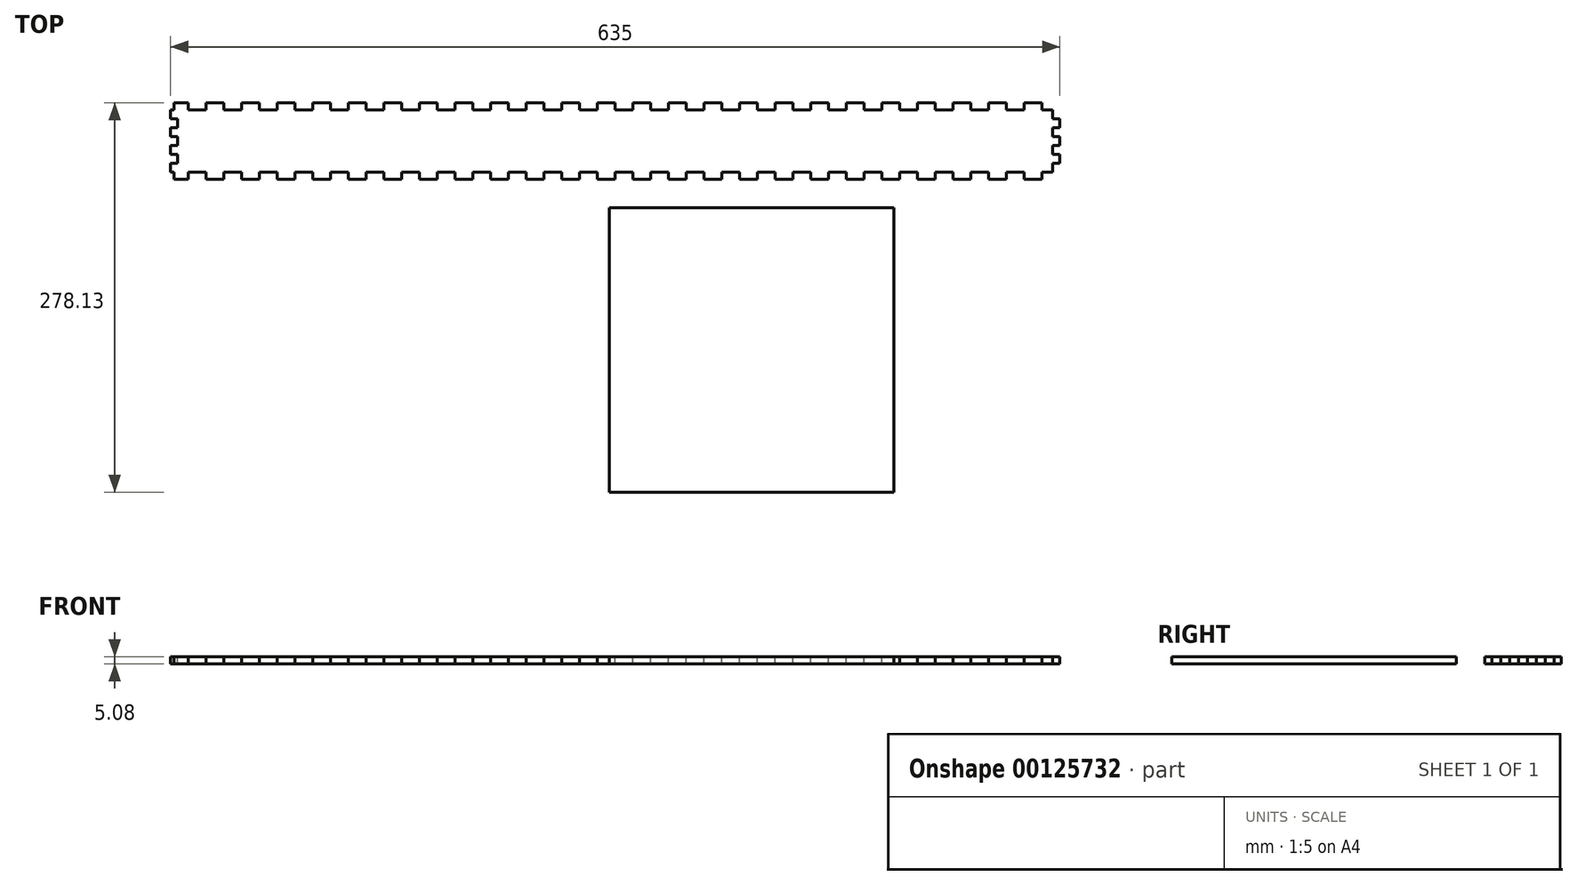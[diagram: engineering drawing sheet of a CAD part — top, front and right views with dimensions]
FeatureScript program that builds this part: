
annotation { "Feature Type Name" : "Feature", "Feature Type Description" : "" }
export const myFeature = defineFeature(function(context is Context, id is Id, definition is map)
    precondition{}
    {
        {
            var Q0;
            Q0=qCreatedBy(makeId("Top.planeOp"),FACE);
            var sketch = newSketch(context, id + "F0", { "sketchPlane" : qUnion([Q0])});
            skLineSegment(sketch, "E0.bottom", {"start": v(-540.54, 29.9) * mm, "end": v(94.46, 29.9) * mm});
            skLineSegment(sketch, "E0.top", {"start": v(-540.54, -24.7) * mm, "end": v(94.46, -24.7) * mm});
            skLineSegment(sketch, "E0.left", {"start": v(-540.54, 29.9) * mm, "end": v(-540.54, -24.7) * mm});
            skLineSegment(sketch, "E0.right", {"start": v(94.46, 29.9) * mm, "end": v(94.46, -24.7) * mm});
            skSolve(sketch);
        }
        {
            var Q0;
            Q0=makeQuery(id+"F0.imprint","IMPRINT",FACE,{"disambiguationData":[TD([[makeQuery(id+"F0.imprint","IMPRINT",EDGE,{"derivedFrom":sQuery(id+"F0.wireOp",EDGE,"E0.bottom")}),-1.0]])]});
            extrude(context, id + "F1", {"entities" : qUnion([Q0]), "depth" : 5.08 * mm});
        }
        {
            var Q0;
            Q0=makeQuery(id+"F1.opExtrude","CAP_FACE",FACE,{"disambiguationData":[OSD([sQuery(id+"F0.wireOp",EDGE,"E0.bottom"),sQuery(id+"F0.wireOp",EDGE,"E0.top"),sQuery(id+"F0.wireOp",EDGE,"E0.left"),sQuery(id+"F0.wireOp",EDGE,"E0.right")])],"isStart":false});
            var sketch = newSketch(context, id + "F2", { "sketchPlane" : qUnion([Q0])});
            skLineSegment(sketch, "E1.0", {"start": v(-540.54, 29.9) * mm, "end": v(94.46, 29.9) * mm});
            skLineSegment(sketch, "E1.1", {"start": v(-540.54, 29.9) * mm, "end": v(-540.54, -24.7) * mm});
            skLineSegment(sketch, "E2", {"start": v(-527.84, 29.9) * mm, "end": v(-527.84, 24.83) * mm});
            skLineSegment(sketch, "E3", {"start": v(-527.84, 24.83) * mm, "end": v(-515.14, 24.83) * mm});
            skLineSegment(sketch, "E4", {"start": v(-515.14, 24.83) * mm, "end": v(-515.14, 29.9) * mm});
            skLineSegment(sketch, "E5.1.0.0", {"start": v(-502.44, 29.9) * mm, "end": v(-502.44, 24.83) * mm});
            skLineSegment(sketch, "E5.1.0.1", {"start": v(-502.44, 24.83) * mm, "end": v(-489.74, 24.83) * mm});
            skLineSegment(sketch, "E5.1.0.2", {"start": v(-489.74, 24.83) * mm, "end": v(-489.74, 29.9) * mm});
            skLineSegment(sketch, "E5.2.0.0", {"start": v(-477.04, 29.9) * mm, "end": v(-477.04, 24.83) * mm});
            skLineSegment(sketch, "E5.2.0.1", {"start": v(-477.04, 24.83) * mm, "end": v(-464.34, 24.83) * mm});
            skLineSegment(sketch, "E5.2.0.2", {"start": v(-464.34, 24.83) * mm, "end": v(-464.34, 29.9) * mm});
            skLineSegment(sketch, "E5.3.0.0", {"start": v(-451.64, 29.9) * mm, "end": v(-451.64, 24.83) * mm});
            skLineSegment(sketch, "E5.3.0.1", {"start": v(-451.64, 24.83) * mm, "end": v(-438.94, 24.83) * mm});
            skLineSegment(sketch, "E5.3.0.2", {"start": v(-438.94, 24.83) * mm, "end": v(-438.94, 29.9) * mm});
            skLineSegment(sketch, "E5.4.0.0", {"start": v(-426.24, 29.9) * mm, "end": v(-426.24, 24.83) * mm});
            skLineSegment(sketch, "E5.4.0.1", {"start": v(-426.24, 24.83) * mm, "end": v(-413.54, 24.83) * mm});
            skLineSegment(sketch, "E5.4.0.2", {"start": v(-413.54, 24.83) * mm, "end": v(-413.54, 29.9) * mm});
            skLineSegment(sketch, "E5.5.0.0", {"start": v(-400.84, 29.9) * mm, "end": v(-400.84, 24.83) * mm});
            skLineSegment(sketch, "E5.5.0.1", {"start": v(-400.84, 24.83) * mm, "end": v(-388.14, 24.83) * mm});
            skLineSegment(sketch, "E5.5.0.2", {"start": v(-388.14, 24.83) * mm, "end": v(-388.14, 29.9) * mm});
            skLineSegment(sketch, "E5.6.0.0", {"start": v(-375.44, 29.9) * mm, "end": v(-375.44, 24.83) * mm});
            skLineSegment(sketch, "E5.6.0.1", {"start": v(-375.44, 24.83) * mm, "end": v(-362.74, 24.83) * mm});
            skLineSegment(sketch, "E5.6.0.2", {"start": v(-362.74, 24.83) * mm, "end": v(-362.74, 29.9) * mm});
            skLineSegment(sketch, "E5.7.0.0", {"start": v(-350.04, 29.9) * mm, "end": v(-350.04, 24.83) * mm});
            skLineSegment(sketch, "E5.7.0.1", {"start": v(-350.04, 24.83) * mm, "end": v(-337.34, 24.83) * mm});
            skLineSegment(sketch, "E5.7.0.2", {"start": v(-337.34, 24.83) * mm, "end": v(-337.34, 29.9) * mm});
            skLineSegment(sketch, "E5.8.0.0", {"start": v(-324.64, 29.9) * mm, "end": v(-324.64, 24.83) * mm});
            skLineSegment(sketch, "E5.8.0.1", {"start": v(-324.64, 24.83) * mm, "end": v(-311.94, 24.83) * mm});
            skLineSegment(sketch, "E5.8.0.2", {"start": v(-311.94, 24.83) * mm, "end": v(-311.94, 29.9) * mm});
            skLineSegment(sketch, "E5.9.0.0", {"start": v(-299.24, 29.9) * mm, "end": v(-299.24, 24.83) * mm});
            skLineSegment(sketch, "E5.9.0.1", {"start": v(-299.24, 24.83) * mm, "end": v(-286.54, 24.83) * mm});
            skLineSegment(sketch, "E5.9.0.2", {"start": v(-286.54, 24.83) * mm, "end": v(-286.54, 29.9) * mm});
            skLineSegment(sketch, "E5.10.0.0", {"start": v(-273.84, 29.9) * mm, "end": v(-273.84, 24.83) * mm});
            skLineSegment(sketch, "E5.10.0.1", {"start": v(-273.84, 24.83) * mm, "end": v(-261.14, 24.83) * mm});
            skLineSegment(sketch, "E5.10.0.2", {"start": v(-261.14, 24.83) * mm, "end": v(-261.14, 29.9) * mm});
            skLineSegment(sketch, "E5.11.0.0", {"start": v(-248.44, 29.9) * mm, "end": v(-248.44, 24.83) * mm});
            skLineSegment(sketch, "E5.11.0.1", {"start": v(-248.44, 24.83) * mm, "end": v(-235.74, 24.83) * mm});
            skLineSegment(sketch, "E5.11.0.2", {"start": v(-235.74, 24.83) * mm, "end": v(-235.74, 29.9) * mm});
            skLineSegment(sketch, "E5.12.0.0", {"start": v(-223.04, 29.9) * mm, "end": v(-223.04, 24.83) * mm});
            skLineSegment(sketch, "E5.12.0.1", {"start": v(-223.04, 24.83) * mm, "end": v(-210.34, 24.83) * mm});
            skLineSegment(sketch, "E5.12.0.2", {"start": v(-210.34, 24.83) * mm, "end": v(-210.34, 29.9) * mm});
            skLineSegment(sketch, "E5.13.0.0", {"start": v(-197.64, 29.9) * mm, "end": v(-197.64, 24.83) * mm});
            skLineSegment(sketch, "E5.13.0.1", {"start": v(-197.64, 24.83) * mm, "end": v(-184.94, 24.83) * mm});
            skLineSegment(sketch, "E5.13.0.2", {"start": v(-184.94, 24.83) * mm, "end": v(-184.94, 29.9) * mm});
            skLineSegment(sketch, "E5.14.0.0", {"start": v(-172.24, 29.9) * mm, "end": v(-172.24, 24.83) * mm});
            skLineSegment(sketch, "E5.14.0.1", {"start": v(-172.24, 24.83) * mm, "end": v(-159.54, 24.83) * mm});
            skLineSegment(sketch, "E5.14.0.2", {"start": v(-159.54, 24.83) * mm, "end": v(-159.54, 29.9) * mm});
            skLineSegment(sketch, "E5.15.0.0", {"start": v(-146.84, 29.9) * mm, "end": v(-146.84, 24.83) * mm});
            skLineSegment(sketch, "E5.15.0.1", {"start": v(-146.84, 24.83) * mm, "end": v(-134.14, 24.83) * mm});
            skLineSegment(sketch, "E5.15.0.2", {"start": v(-134.14, 24.83) * mm, "end": v(-134.14, 29.9) * mm});
            skLineSegment(sketch, "E5.16.0.0", {"start": v(-121.44, 29.9) * mm, "end": v(-121.44, 24.83) * mm});
            skLineSegment(sketch, "E5.16.0.1", {"start": v(-121.44, 24.83) * mm, "end": v(-108.74, 24.83) * mm});
            skLineSegment(sketch, "E5.16.0.2", {"start": v(-108.74, 24.83) * mm, "end": v(-108.74, 29.9) * mm});
            skLineSegment(sketch, "E5.17.0.0", {"start": v(-96.04, 29.9) * mm, "end": v(-96.04, 24.83) * mm});
            skLineSegment(sketch, "E5.17.0.1", {"start": v(-96.04, 24.83) * mm, "end": v(-83.34, 24.83) * mm});
            skLineSegment(sketch, "E5.17.0.2", {"start": v(-83.34, 24.83) * mm, "end": v(-83.34, 29.9) * mm});
            skLineSegment(sketch, "E5.18.0.0", {"start": v(-70.64, 29.9) * mm, "end": v(-70.64, 24.83) * mm});
            skLineSegment(sketch, "E5.18.0.1", {"start": v(-70.64, 24.83) * mm, "end": v(-57.94, 24.83) * mm});
            skLineSegment(sketch, "E5.18.0.2", {"start": v(-57.94, 24.83) * mm, "end": v(-57.94, 29.9) * mm});
            skLineSegment(sketch, "E5.19.0.0", {"start": v(-45.24, 29.9) * mm, "end": v(-45.24, 24.83) * mm});
            skLineSegment(sketch, "E5.19.0.1", {"start": v(-45.24, 24.83) * mm, "end": v(-32.54, 24.83) * mm});
            skLineSegment(sketch, "E5.19.0.2", {"start": v(-32.54, 24.83) * mm, "end": v(-32.54, 29.9) * mm});
            skLineSegment(sketch, "E5.20.0.0", {"start": v(-19.84, 29.9) * mm, "end": v(-19.84, 24.83) * mm});
            skLineSegment(sketch, "E5.20.0.1", {"start": v(-19.84, 24.83) * mm, "end": v(-7.14, 24.83) * mm});
            skLineSegment(sketch, "E5.20.0.2", {"start": v(-7.14, 24.83) * mm, "end": v(-7.14, 29.9) * mm});
            skLineSegment(sketch, "E5.21.0.0", {"start": v(5.56, 29.9) * mm, "end": v(5.56, 24.83) * mm});
            skLineSegment(sketch, "E5.21.0.1", {"start": v(5.56, 24.83) * mm, "end": v(18.26, 24.83) * mm});
            skLineSegment(sketch, "E5.21.0.2", {"start": v(18.26, 24.83) * mm, "end": v(18.26, 29.9) * mm});
            skLineSegment(sketch, "E5.22.0.0", {"start": v(30.96, 29.9) * mm, "end": v(30.96, 24.83) * mm});
            skLineSegment(sketch, "E5.22.0.1", {"start": v(30.96, 24.83) * mm, "end": v(43.66, 24.83) * mm});
            skLineSegment(sketch, "E5.22.0.2", {"start": v(43.66, 24.83) * mm, "end": v(43.66, 29.9) * mm});
            skLineSegment(sketch, "E5.23.0.0", {"start": v(56.36, 29.9) * mm, "end": v(56.36, 24.83) * mm});
            skLineSegment(sketch, "E5.23.0.1", {"start": v(56.36, 24.83) * mm, "end": v(69.06, 24.83) * mm});
            skLineSegment(sketch, "E5.23.0.2", {"start": v(69.06, 24.83) * mm, "end": v(69.06, 29.9) * mm});
            skLineSegment(sketch, "E5.24.0.0", {"start": v(81.76, 29.9) * mm, "end": v(81.76, 24.83) * mm});
            skLineSegment(sketch, "E5.24.0.1", {"start": v(81.76, 24.83) * mm, "end": v(94.46, 24.83) * mm});
            skLineSegment(sketch, "E5.24.0.2", {"start": v(94.46, 24.83) * mm, "end": v(94.46, 29.9) * mm});
            skLineSegment(sketch, "E5.direction1", {"start": v(-527.84, 24.83) * mm, "end": v(-502.44, 24.83) * mm, "construction": true});
            skLineSegment(sketch, "E6", {"start": v(-540.54, 18.48) * mm, "end": v(-535.46, 18.48) * mm});
            skLineSegment(sketch, "E7", {"start": v(-535.46, 18.48) * mm, "end": v(-535.46, 12.13) * mm});
            skLineSegment(sketch, "E8", {"start": v(-535.46, 12.13) * mm, "end": v(-540.54, 12.13) * mm});
            skLineSegment(sketch, "E9.0.1.0", {"start": v(-540.54, 5.78) * mm, "end": v(-535.46, 5.78) * mm});
            skLineSegment(sketch, "E9.0.1.1", {"start": v(-535.46, 5.78) * mm, "end": v(-535.46, -0.57) * mm});
            skLineSegment(sketch, "E9.0.1.2", {"start": v(-535.46, -0.57) * mm, "end": v(-540.54, -0.57) * mm});
            skLineSegment(sketch, "E9.0.2.0", {"start": v(-540.54, -6.92) * mm, "end": v(-535.46, -6.92) * mm});
            skLineSegment(sketch, "E9.0.2.1", {"start": v(-535.46, -6.92) * mm, "end": v(-535.46, -13.27) * mm});
            skLineSegment(sketch, "E9.0.2.2", {"start": v(-535.46, -13.27) * mm, "end": v(-540.54, -13.27) * mm});
            skLineSegment(sketch, "E9.direction1", {"start": v(-540.54, 12.13) * mm, "end": v(-515.14, 12.13) * mm, "construction": true});
            skLineSegment(sketch, "E9.direction2", {"start": v(-540.54, 12.13) * mm, "end": v(-540.54, -0.57) * mm, "construction": true});
            skLineSegment(sketch, "E10", {"start": v(-540.54, 2.6) * mm, "end": v(-455.77, 2.6) * mm, "construction": true});
            skPoint(sketch, "E10.endSnap0", {"position": v(-535.46, 2.6) * mm});
            skLineSegment(sketch, "E11.MirrorCS", {"start": v(-502.44, -24.7) * mm, "end": v(-502.44, -19.62) * mm});
            skLineSegment(sketch, "E12.MirrorCS", {"start": v(-502.44, -19.62) * mm, "end": v(-489.74, -19.62) * mm});
            skLineSegment(sketch, "E13.MirrorCS", {"start": v(-489.74, -19.62) * mm, "end": v(-489.74, -24.7) * mm});
            skLineSegment(sketch, "E14.MirrorCS", {"start": v(-515.14, -19.62) * mm, "end": v(-515.14, -24.7) * mm});
            skLineSegment(sketch, "E15.MirrorCS", {"start": v(-527.84, -24.7) * mm, "end": v(-527.84, -19.62) * mm});
            skLineSegment(sketch, "E16.MirrorCS", {"start": v(-477.04, -24.7) * mm, "end": v(-477.04, -19.62) * mm});
            skLineSegment(sketch, "E17.MirrorCS", {"start": v(-477.04, -19.62) * mm, "end": v(-464.34, -19.62) * mm});
            skLineSegment(sketch, "E18.MirrorCS", {"start": v(-464.34, -19.62) * mm, "end": v(-464.34, -24.7) * mm});
            skLineSegment(sketch, "E19", {"start": v(-527.84, -19.62) * mm, "end": v(-515.14, -19.62) * mm});
            skLineSegment(sketch, "E20.MirrorCS", {"start": v(18.26, -19.62) * mm, "end": v(18.26, -24.7) * mm});
            skLineSegment(sketch, "E21.MirrorCS", {"start": v(-184.94, -19.62) * mm, "end": v(-184.94, -24.7) * mm});
            skLineSegment(sketch, "E22.MirrorCS", {"start": v(-45.24, -24.7) * mm, "end": v(-45.24, -19.62) * mm});
            skLineSegment(sketch, "E23.MirrorCS", {"start": v(-299.24, -24.7) * mm, "end": v(-299.24, -19.62) * mm});
            skLineSegment(sketch, "E24.MirrorCS", {"start": v(-375.44, -24.7) * mm, "end": v(-375.44, -19.62) * mm});
            skLineSegment(sketch, "E25.MirrorCS", {"start": v(-121.44, -24.7) * mm, "end": v(-121.44, -19.62) * mm});
            skLineSegment(sketch, "E26.MirrorCS", {"start": v(-388.14, -19.62) * mm, "end": v(-388.14, -24.7) * mm});
            skLineSegment(sketch, "E27.MirrorCS", {"start": v(-261.14, -19.62) * mm, "end": v(-261.14, -24.7) * mm});
            skLineSegment(sketch, "E28.MirrorCS", {"start": v(-197.64, -24.7) * mm, "end": v(-197.64, -19.62) * mm});
            skLineSegment(sketch, "E29.MirrorCS", {"start": v(-337.34, -19.62) * mm, "end": v(-337.34, -24.7) * mm});
            skLineSegment(sketch, "E30.MirrorCS", {"start": v(69.06, -19.62) * mm, "end": v(69.06, -24.7) * mm});
            skLineSegment(sketch, "E31.MirrorCS", {"start": v(-451.64, -24.7) * mm, "end": v(-451.64, -19.62) * mm});
            skLineSegment(sketch, "E32.MirrorCS", {"start": v(-426.24, -24.7) * mm, "end": v(-426.24, -19.62) * mm});
            skLineSegment(sketch, "E33.MirrorCS", {"start": v(-438.94, -19.62) * mm, "end": v(-438.94, -24.7) * mm});
            skLineSegment(sketch, "E34.MirrorCS", {"start": v(5.56, -24.7) * mm, "end": v(5.56, -19.62) * mm});
            skLineSegment(sketch, "E35.MirrorCS", {"start": v(-134.14, -19.62) * mm, "end": v(-134.14, -24.7) * mm});
            skLineSegment(sketch, "E36.MirrorCS", {"start": v(-400.84, -24.7) * mm, "end": v(-400.84, -19.62) * mm});
            skLineSegment(sketch, "E37.MirrorCS", {"start": v(-210.34, -19.62) * mm, "end": v(-210.34, -24.7) * mm});
            skLineSegment(sketch, "E38.MirrorCS", {"start": v(-70.64, -24.7) * mm, "end": v(-70.64, -19.62) * mm});
            skLineSegment(sketch, "E39.MirrorCS", {"start": v(-413.54, -19.62) * mm, "end": v(-413.54, -24.7) * mm});
            skLineSegment(sketch, "E40.MirrorCS", {"start": v(-273.84, -24.7) * mm, "end": v(-273.84, -19.62) * mm});
            skLineSegment(sketch, "E41.MirrorCS", {"start": v(-350.04, -24.7) * mm, "end": v(-350.04, -19.62) * mm});
            skLineSegment(sketch, "E42.MirrorCS", {"start": v(-83.34, -19.62) * mm, "end": v(-83.34, -24.7) * mm});
            skLineSegment(sketch, "E43.MirrorCS", {"start": v(56.36, -24.7) * mm, "end": v(56.36, -19.62) * mm});
            skLineSegment(sketch, "E44.MirrorCS", {"start": v(-7.14, -19.62) * mm, "end": v(-7.14, -24.7) * mm});
            skLineSegment(sketch, "E45.MirrorCS", {"start": v(43.66, -19.62) * mm, "end": v(43.66, -24.7) * mm});
            skLineSegment(sketch, "E46.MirrorCS", {"start": v(-146.84, -24.7) * mm, "end": v(-146.84, -19.62) * mm});
            skLineSegment(sketch, "E47.MirrorCS", {"start": v(-286.54, -19.62) * mm, "end": v(-286.54, -24.7) * mm});
            skLineSegment(sketch, "E48.MirrorCS", {"start": v(-223.04, -24.7) * mm, "end": v(-223.04, -19.62) * mm});
            skLineSegment(sketch, "E49.MirrorCS", {"start": v(-362.74, -19.62) * mm, "end": v(-362.74, -24.7) * mm});
            skLineSegment(sketch, "E50.MirrorCS", {"start": v(-159.54, -19.62) * mm, "end": v(-159.54, -24.7) * mm});
            skLineSegment(sketch, "E51.MirrorCS", {"start": v(-19.84, -24.7) * mm, "end": v(-19.84, -19.62) * mm});
            skLineSegment(sketch, "E52.MirrorCS", {"start": v(-96.04, -24.7) * mm, "end": v(-96.04, -19.62) * mm});
            skLineSegment(sketch, "E53.MirrorCS", {"start": v(-248.44, -24.7) * mm, "end": v(-248.44, -19.62) * mm});
            skLineSegment(sketch, "E54.MirrorCS", {"start": v(81.76, -24.7) * mm, "end": v(81.76, -19.62) * mm});
            skLineSegment(sketch, "E55.MirrorCS", {"start": v(-311.94, -19.62) * mm, "end": v(-311.94, -24.7) * mm});
            skLineSegment(sketch, "E56.MirrorCS", {"start": v(-235.74, -19.62) * mm, "end": v(-235.74, -24.7) * mm});
            skLineSegment(sketch, "E57.MirrorCS", {"start": v(-172.24, -24.7) * mm, "end": v(-172.24, -19.62) * mm});
            skLineSegment(sketch, "E58.MirrorCS", {"start": v(-57.94, -19.62) * mm, "end": v(-57.94, -24.7) * mm});
            skLineSegment(sketch, "E59.MirrorCS", {"start": v(94.46, -19.62) * mm, "end": v(94.46, -24.7) * mm});
            skLineSegment(sketch, "E60.MirrorCS", {"start": v(-324.64, -24.7) * mm, "end": v(-324.64, -19.62) * mm});
            skLineSegment(sketch, "E61.MirrorCS", {"start": v(-108.74, -19.62) * mm, "end": v(-108.74, -24.7) * mm});
            skLineSegment(sketch, "E62.MirrorCS", {"start": v(30.96, -24.7) * mm, "end": v(30.96, -19.62) * mm});
            skLineSegment(sketch, "E63.MirrorCS", {"start": v(-32.54, -19.62) * mm, "end": v(-32.54, -24.7) * mm});
            skLineSegment(sketch, "E64.MirrorCS", {"start": v(-121.44, -19.62) * mm, "end": v(-108.74, -19.62) * mm});
            skLineSegment(sketch, "E65.MirrorCS", {"start": v(-324.64, -19.62) * mm, "end": v(-311.94, -19.62) * mm});
            skLineSegment(sketch, "E66.MirrorCS", {"start": v(-248.44, -19.62) * mm, "end": v(-235.74, -19.62) * mm});
            skLineSegment(sketch, "E67.MirrorCS", {"start": v(5.56, -19.62) * mm, "end": v(18.26, -19.62) * mm});
            skLineSegment(sketch, "E68.MirrorCS", {"start": v(-400.84, -19.62) * mm, "end": v(-388.14, -19.62) * mm});
            skLineSegment(sketch, "E69.MirrorCS", {"start": v(-451.64, -19.62) * mm, "end": v(-438.94, -19.62) * mm});
            skLineSegment(sketch, "E70.MirrorCS", {"start": v(-70.64, -19.62) * mm, "end": v(-57.94, -19.62) * mm});
            skLineSegment(sketch, "E71.MirrorCS", {"start": v(-426.24, -19.62) * mm, "end": v(-413.54, -19.62) * mm});
            skLineSegment(sketch, "E72.MirrorCS", {"start": v(-273.84, -19.62) * mm, "end": v(-261.14, -19.62) * mm});
            skLineSegment(sketch, "E73.MirrorCS", {"start": v(-350.04, -19.62) * mm, "end": v(-337.34, -19.62) * mm});
            skLineSegment(sketch, "E74.MirrorCS", {"start": v(56.36, -19.62) * mm, "end": v(69.06, -19.62) * mm});
            skLineSegment(sketch, "E75.MirrorCS", {"start": v(-223.04, -19.62) * mm, "end": v(-210.34, -19.62) * mm});
            skLineSegment(sketch, "E76.MirrorCS", {"start": v(-146.84, -19.62) * mm, "end": v(-134.14, -19.62) * mm});
            skLineSegment(sketch, "E77.MirrorCS", {"start": v(-96.04, -19.62) * mm, "end": v(-83.34, -19.62) * mm});
            skLineSegment(sketch, "E78.MirrorCS", {"start": v(-19.84, -19.62) * mm, "end": v(-7.14, -19.62) * mm});
            skLineSegment(sketch, "E79.MirrorCS", {"start": v(81.76, -19.62) * mm, "end": v(94.46, -19.62) * mm});
            skLineSegment(sketch, "E80.MirrorCS", {"start": v(30.96, -19.62) * mm, "end": v(43.66, -19.62) * mm});
            skLineSegment(sketch, "E81.MirrorCS", {"start": v(-375.44, -19.62) * mm, "end": v(-362.74, -19.62) * mm});
            skLineSegment(sketch, "E82.MirrorCS", {"start": v(-299.24, -19.62) * mm, "end": v(-286.54, -19.62) * mm});
            skLineSegment(sketch, "E83.MirrorCS", {"start": v(-45.24, -19.62) * mm, "end": v(-32.54, -19.62) * mm});
            skLineSegment(sketch, "E84.MirrorCS", {"start": v(-172.24, -19.62) * mm, "end": v(-159.54, -19.62) * mm});
            skLineSegment(sketch, "E85.MirrorCS", {"start": v(-197.64, -19.62) * mm, "end": v(-184.94, -19.62) * mm});
            skLineSegment(sketch, "E86", {"start": v(-223.04, 29.9) * mm, "end": v(-223.04, -38.72) * mm, "construction": true});
            skLineSegment(sketch, "E87.MirrorCS", {"start": v(89.38, -13.27) * mm, "end": v(94.46, -13.27) * mm});
            skLineSegment(sketch, "E88.MirrorCS", {"start": v(94.46, -6.92) * mm, "end": v(89.38, -6.92) * mm});
            skLineSegment(sketch, "E89.MirrorCS", {"start": v(89.38, -0.57) * mm, "end": v(94.46, -0.57) * mm});
            skLineSegment(sketch, "E90.MirrorCS", {"start": v(94.46, 5.78) * mm, "end": v(89.38, 5.78) * mm});
            skLineSegment(sketch, "E91.MirrorCS", {"start": v(94.46, 18.48) * mm, "end": v(89.38, 18.48) * mm});
            skLineSegment(sketch, "E92", {"start": v(89.38, 12.13) * mm, "end": v(94.46, 12.13) * mm});
            skLineSegment(sketch, "E93", {"start": v(89.38, 12.13) * mm, "end": v(89.38, 5.78) * mm});
            skLineSegment(sketch, "E94", {"start": v(89.38, -0.57) * mm, "end": v(89.38, -6.92) * mm});
            skLineSegment(sketch, "E95", {"start": v(89.38, -13.27) * mm, "end": v(89.38, -19.62) * mm});
            skLineSegment(sketch, "E96", {"start": v(89.38, 18.48) * mm, "end": v(89.38, 24.83) * mm});
            skLineSegment(sketch, "E97", {"start": v(-464.34, -24.7) * mm, "end": v(-451.64, -24.7) * mm});
            skLineSegment(sketch, "E98", {"start": v(-538, 29.9) * mm, "end": v(-538, 24.83) * mm});
            skLineSegment(sketch, "E99", {"start": v(-538, 24.83) * mm, "end": v(-540.54, 24.83) * mm});
            skLineSegment(sketch, "E100.MirrorCS", {"start": v(-538, -24.7) * mm, "end": v(-538, -19.62) * mm});
            skLineSegment(sketch, "E101.MirrorCS", {"start": v(-538, -19.62) * mm, "end": v(-540.54, -19.62) * mm});
            skSolve(sketch);
        }
        {
            var Q0;
            {var subQ0=sQuery(id+"F2.wireOp",EDGE,"E6");Q0=makeQuery(id+"F2.imprint","IMPRINT",FACE,{"disambiguationData":[TD([[makeQuery(id+"F2.imprint","IMPRINT",EDGE,{"derivedFrom":subQ0}),-1.0]])]});}
            var Q1;
            {var subQ0=sQuery(id+"F2.wireOp",EDGE,"E9.0.1.0");Q1=makeQuery(id+"F2.imprint","IMPRINT",FACE,{"disambiguationData":[TD([[makeQuery(id+"F2.imprint","IMPRINT",EDGE,{"derivedFrom":subQ0}),-1.0]])]});}
            var Q2;
            {var subQ0=sQuery(id+"F2.wireOp",EDGE,"E9.0.2.0");Q2=makeQuery(id+"F2.imprint","IMPRINT",FACE,{"disambiguationData":[TD([[makeQuery(id+"F2.imprint","IMPRINT",EDGE,{"derivedFrom":subQ0}),-1.0]])]});}
            var Q3;
            {var subQ0=sQuery(id+"F2.wireOp",EDGE,"E2");Q3=makeQuery(id+"F2.imprint","IMPRINT",FACE,{"disambiguationData":[TD([[makeQuery(id+"F2.imprint","IMPRINT",EDGE,{"derivedFrom":subQ0}),1.0]])]});}
            var Q4;
            {var subQ0=sQuery(id+"F2.wireOp",EDGE,"E5.1.0.0");Q4=makeQuery(id+"F2.imprint","IMPRINT",FACE,{"disambiguationData":[TD([[makeQuery(id+"F2.imprint","IMPRINT",EDGE,{"derivedFrom":subQ0}),1.0]])]});}
            var Q5;
            {var subQ0=sQuery(id+"F2.wireOp",EDGE,"E14.MirrorCS");Q5=makeQuery(id+"F2.imprint","IMPRINT",FACE,{"disambiguationData":[TD([[makeQuery(id+"F2.imprint","IMPRINT",EDGE,{"derivedFrom":subQ0}),-1.0]])]});}
            var Q6;
            {var subQ0=sQuery(id+"F2.wireOp",EDGE,"E11.MirrorCS");Q6=makeQuery(id+"F2.imprint","IMPRINT",FACE,{"disambiguationData":[TD([[makeQuery(id+"F2.imprint","IMPRINT",EDGE,{"derivedFrom":subQ0}),-1.0]])]});}
            var Q7;
            {var subQ0=sQuery(id+"F2.wireOp",EDGE,"E5.2.0.0");Q7=makeQuery(id+"F2.imprint","IMPRINT",FACE,{"disambiguationData":[TD([[makeQuery(id+"F2.imprint","IMPRINT",EDGE,{"derivedFrom":subQ0}),1.0]])]});}
            var Q8;
            {var subQ0=sQuery(id+"F2.wireOp",EDGE,"E16.MirrorCS");Q8=makeQuery(id+"F2.imprint","IMPRINT",FACE,{"disambiguationData":[TD([[makeQuery(id+"F2.imprint","IMPRINT",EDGE,{"derivedFrom":subQ0}),-1.0]])]});}
            var Q9;
            {var subQ0=sQuery(id+"F2.wireOp",EDGE,"E31.MirrorCS");Q9=makeQuery(id+"F2.imprint","IMPRINT",FACE,{"disambiguationData":[TD([[makeQuery(id+"F2.imprint","IMPRINT",EDGE,{"derivedFrom":subQ0}),-1.0]])]});}
            var Q10;
            {var subQ0=sQuery(id+"F2.wireOp",EDGE,"E5.3.0.0");Q10=makeQuery(id+"F2.imprint","IMPRINT",FACE,{"disambiguationData":[TD([[makeQuery(id+"F2.imprint","IMPRINT",EDGE,{"derivedFrom":subQ0}),1.0]])]});}
            var Q11;
            {var subQ0=sQuery(id+"F2.wireOp",EDGE,"E5.4.0.0");Q11=makeQuery(id+"F2.imprint","IMPRINT",FACE,{"disambiguationData":[TD([[makeQuery(id+"F2.imprint","IMPRINT",EDGE,{"derivedFrom":subQ0}),1.0]])]});}
            var Q12;
            {var subQ0=sQuery(id+"F2.wireOp",EDGE,"E32.MirrorCS");Q12=makeQuery(id+"F2.imprint","IMPRINT",FACE,{"disambiguationData":[TD([[makeQuery(id+"F2.imprint","IMPRINT",EDGE,{"derivedFrom":subQ0}),-1.0]])]});}
            var Q13;
            {var subQ0=sQuery(id+"F2.wireOp",EDGE,"E26.MirrorCS");Q13=makeQuery(id+"F2.imprint","IMPRINT",FACE,{"disambiguationData":[TD([[makeQuery(id+"F2.imprint","IMPRINT",EDGE,{"derivedFrom":subQ0}),-1.0]])]});}
            var Q14;
            {var subQ0=sQuery(id+"F2.wireOp",EDGE,"E5.5.0.0");Q14=makeQuery(id+"F2.imprint","IMPRINT",FACE,{"disambiguationData":[TD([[makeQuery(id+"F2.imprint","IMPRINT",EDGE,{"derivedFrom":subQ0}),1.0]])]});}
            var Q15;
            {var subQ0=sQuery(id+"F2.wireOp",EDGE,"E5.6.0.0");Q15=makeQuery(id+"F2.imprint","IMPRINT",FACE,{"disambiguationData":[TD([[makeQuery(id+"F2.imprint","IMPRINT",EDGE,{"derivedFrom":subQ0}),1.0]])]});}
            var Q16;
            {var subQ0=sQuery(id+"F2.wireOp",EDGE,"E24.MirrorCS");Q16=makeQuery(id+"F2.imprint","IMPRINT",FACE,{"disambiguationData":[TD([[makeQuery(id+"F2.imprint","IMPRINT",EDGE,{"derivedFrom":subQ0}),-1.0]])]});}
            var Q17;
            {var subQ0=sQuery(id+"F2.wireOp",EDGE,"E29.MirrorCS");Q17=makeQuery(id+"F2.imprint","IMPRINT",FACE,{"disambiguationData":[TD([[makeQuery(id+"F2.imprint","IMPRINT",EDGE,{"derivedFrom":subQ0}),-1.0]])]});}
            var Q18;
            {var subQ0=sQuery(id+"F2.wireOp",EDGE,"E5.7.0.0");Q18=makeQuery(id+"F2.imprint","IMPRINT",FACE,{"disambiguationData":[TD([[makeQuery(id+"F2.imprint","IMPRINT",EDGE,{"derivedFrom":subQ0}),1.0]])]});}
            var Q19;
            {var subQ0=sQuery(id+"F2.wireOp",EDGE,"E5.8.0.0");Q19=makeQuery(id+"F2.imprint","IMPRINT",FACE,{"disambiguationData":[TD([[makeQuery(id+"F2.imprint","IMPRINT",EDGE,{"derivedFrom":subQ0}),1.0]])]});}
            var Q20;
            {var subQ0=sQuery(id+"F2.wireOp",EDGE,"E55.MirrorCS");Q20=makeQuery(id+"F2.imprint","IMPRINT",FACE,{"disambiguationData":[TD([[makeQuery(id+"F2.imprint","IMPRINT",EDGE,{"derivedFrom":subQ0}),-1.0]])]});}
            var Q21;
            {var subQ0=sQuery(id+"F2.wireOp",EDGE,"E23.MirrorCS");Q21=makeQuery(id+"F2.imprint","IMPRINT",FACE,{"disambiguationData":[TD([[makeQuery(id+"F2.imprint","IMPRINT",EDGE,{"derivedFrom":subQ0}),-1.0]])]});}
            var Q22;
            {var subQ0=sQuery(id+"F2.wireOp",EDGE,"E5.9.0.0");Q22=makeQuery(id+"F2.imprint","IMPRINT",FACE,{"disambiguationData":[TD([[makeQuery(id+"F2.imprint","IMPRINT",EDGE,{"derivedFrom":subQ0}),1.0]])]});}
            var Q23;
            {var subQ0=sQuery(id+"F2.wireOp",EDGE,"E5.10.0.0");Q23=makeQuery(id+"F2.imprint","IMPRINT",FACE,{"disambiguationData":[TD([[makeQuery(id+"F2.imprint","IMPRINT",EDGE,{"derivedFrom":subQ0}),1.0]])]});}
            var Q24;
            {var subQ0=sQuery(id+"F2.wireOp",EDGE,"E27.MirrorCS");Q24=makeQuery(id+"F2.imprint","IMPRINT",FACE,{"disambiguationData":[TD([[makeQuery(id+"F2.imprint","IMPRINT",EDGE,{"derivedFrom":subQ0}),-1.0]])]});}
            var Q25;
            {var subQ0=sQuery(id+"F2.wireOp",EDGE,"E53.MirrorCS");Q25=makeQuery(id+"F2.imprint","IMPRINT",FACE,{"disambiguationData":[TD([[makeQuery(id+"F2.imprint","IMPRINT",EDGE,{"derivedFrom":subQ0}),-1.0]])]});}
            var Q26;
            {var subQ0=sQuery(id+"F2.wireOp",EDGE,"E5.11.0.0");Q26=makeQuery(id+"F2.imprint","IMPRINT",FACE,{"disambiguationData":[TD([[makeQuery(id+"F2.imprint","IMPRINT",EDGE,{"derivedFrom":subQ0}),1.0]])]});}
            var Q27;
            {var subQ0=sQuery(id+"F2.wireOp",EDGE,"E5.12.0.0");Q27=makeQuery(id+"F2.imprint","IMPRINT",FACE,{"disambiguationData":[TD([[makeQuery(id+"F2.imprint","IMPRINT",EDGE,{"derivedFrom":subQ0}),1.0]])]});}
            var Q28;
            {var subQ0=sQuery(id+"F2.wireOp",EDGE,"E37.MirrorCS");Q28=makeQuery(id+"F2.imprint","IMPRINT",FACE,{"disambiguationData":[TD([[makeQuery(id+"F2.imprint","IMPRINT",EDGE,{"derivedFrom":subQ0}),-1.0]])]});}
            var Q29;
            {var subQ0=sQuery(id+"F2.wireOp",EDGE,"E5.13.0.0");Q29=makeQuery(id+"F2.imprint","IMPRINT",FACE,{"disambiguationData":[TD([[makeQuery(id+"F2.imprint","IMPRINT",EDGE,{"derivedFrom":subQ0}),1.0]])]});}
            var Q30;
            {var subQ0=sQuery(id+"F2.wireOp",EDGE,"E21.MirrorCS");Q30=makeQuery(id+"F2.imprint","IMPRINT",FACE,{"disambiguationData":[TD([[makeQuery(id+"F2.imprint","IMPRINT",EDGE,{"derivedFrom":subQ0}),-1.0]])]});}
            var Q31;
            {var subQ0=sQuery(id+"F2.wireOp",EDGE,"E50.MirrorCS");Q31=makeQuery(id+"F2.imprint","IMPRINT",FACE,{"disambiguationData":[TD([[makeQuery(id+"F2.imprint","IMPRINT",EDGE,{"derivedFrom":subQ0}),-1.0]])]});}
            var Q32;
            {var subQ0=sQuery(id+"F2.wireOp",EDGE,"E5.14.0.0");Q32=makeQuery(id+"F2.imprint","IMPRINT",FACE,{"disambiguationData":[TD([[makeQuery(id+"F2.imprint","IMPRINT",EDGE,{"derivedFrom":subQ0}),1.0]])]});}
            var Q33;
            {var subQ0=sQuery(id+"F2.wireOp",EDGE,"E5.15.0.0");Q33=makeQuery(id+"F2.imprint","IMPRINT",FACE,{"disambiguationData":[TD([[makeQuery(id+"F2.imprint","IMPRINT",EDGE,{"derivedFrom":subQ0}),1.0]])]});}
            var Q34;
            {var subQ0=sQuery(id+"F2.wireOp",EDGE,"E35.MirrorCS");Q34=makeQuery(id+"F2.imprint","IMPRINT",FACE,{"disambiguationData":[TD([[makeQuery(id+"F2.imprint","IMPRINT",EDGE,{"derivedFrom":subQ0}),-1.0]])]});}
            var Q35;
            {var subQ0=sQuery(id+"F2.wireOp",EDGE,"E25.MirrorCS");Q35=makeQuery(id+"F2.imprint","IMPRINT",FACE,{"disambiguationData":[TD([[makeQuery(id+"F2.imprint","IMPRINT",EDGE,{"derivedFrom":subQ0}),-1.0]])]});}
            var Q36;
            {var subQ0=sQuery(id+"F2.wireOp",EDGE,"E5.16.0.0");Q36=makeQuery(id+"F2.imprint","IMPRINT",FACE,{"disambiguationData":[TD([[makeQuery(id+"F2.imprint","IMPRINT",EDGE,{"derivedFrom":subQ0}),1.0]])]});}
            var Q37;
            {var subQ0=sQuery(id+"F2.wireOp",EDGE,"E42.MirrorCS");Q37=makeQuery(id+"F2.imprint","IMPRINT",FACE,{"disambiguationData":[TD([[makeQuery(id+"F2.imprint","IMPRINT",EDGE,{"derivedFrom":subQ0}),-1.0]])]});}
            var Q38;
            {var subQ0=sQuery(id+"F2.wireOp",EDGE,"E5.17.0.0");Q38=makeQuery(id+"F2.imprint","IMPRINT",FACE,{"disambiguationData":[TD([[makeQuery(id+"F2.imprint","IMPRINT",EDGE,{"derivedFrom":subQ0}),1.0]])]});}
            var Q39;
            {var subQ0=sQuery(id+"F2.wireOp",EDGE,"E38.MirrorCS");Q39=makeQuery(id+"F2.imprint","IMPRINT",FACE,{"disambiguationData":[TD([[makeQuery(id+"F2.imprint","IMPRINT",EDGE,{"derivedFrom":subQ0}),-1.0]])]});}
            var Q40;
            {var subQ0=sQuery(id+"F2.wireOp",EDGE,"E5.18.0.0");Q40=makeQuery(id+"F2.imprint","IMPRINT",FACE,{"disambiguationData":[TD([[makeQuery(id+"F2.imprint","IMPRINT",EDGE,{"derivedFrom":subQ0}),1.0]])]});}
            var Q41;
            {var subQ0=sQuery(id+"F2.wireOp",EDGE,"E5.19.0.0");Q41=makeQuery(id+"F2.imprint","IMPRINT",FACE,{"disambiguationData":[TD([[makeQuery(id+"F2.imprint","IMPRINT",EDGE,{"derivedFrom":subQ0}),1.0]])]});}
            var Q42;
            {var subQ0=sQuery(id+"F2.wireOp",EDGE,"E22.MirrorCS");Q42=makeQuery(id+"F2.imprint","IMPRINT",FACE,{"disambiguationData":[TD([[makeQuery(id+"F2.imprint","IMPRINT",EDGE,{"derivedFrom":subQ0}),-1.0]])]});}
            var Q43;
            {var subQ0=sQuery(id+"F2.wireOp",EDGE,"E44.MirrorCS");Q43=makeQuery(id+"F2.imprint","IMPRINT",FACE,{"disambiguationData":[TD([[makeQuery(id+"F2.imprint","IMPRINT",EDGE,{"derivedFrom":subQ0}),-1.0]])]});}
            var Q44;
            {var subQ0=sQuery(id+"F2.wireOp",EDGE,"E5.20.0.0");Q44=makeQuery(id+"F2.imprint","IMPRINT",FACE,{"disambiguationData":[TD([[makeQuery(id+"F2.imprint","IMPRINT",EDGE,{"derivedFrom":subQ0}),1.0]])]});}
            var Q45;
            {var subQ0=sQuery(id+"F2.wireOp",EDGE,"E5.21.0.0");Q45=makeQuery(id+"F2.imprint","IMPRINT",FACE,{"disambiguationData":[TD([[makeQuery(id+"F2.imprint","IMPRINT",EDGE,{"derivedFrom":subQ0}),1.0]])]});}
            var Q46;
            {var subQ0=sQuery(id+"F2.wireOp",EDGE,"E20.MirrorCS");Q46=makeQuery(id+"F2.imprint","IMPRINT",FACE,{"disambiguationData":[TD([[makeQuery(id+"F2.imprint","IMPRINT",EDGE,{"derivedFrom":subQ0}),-1.0]])]});}
            var Q47;
            {var subQ0=sQuery(id+"F2.wireOp",EDGE,"E45.MirrorCS");Q47=makeQuery(id+"F2.imprint","IMPRINT",FACE,{"disambiguationData":[TD([[makeQuery(id+"F2.imprint","IMPRINT",EDGE,{"derivedFrom":subQ0}),-1.0]])]});}
            var Q48;
            {var subQ0=sQuery(id+"F2.wireOp",EDGE,"E5.22.0.0");Q48=makeQuery(id+"F2.imprint","IMPRINT",FACE,{"disambiguationData":[TD([[makeQuery(id+"F2.imprint","IMPRINT",EDGE,{"derivedFrom":subQ0}),1.0]])]});}
            var Q49;
            {var subQ0=sQuery(id+"F2.wireOp",EDGE,"E5.23.0.0");Q49=makeQuery(id+"F2.imprint","IMPRINT",FACE,{"disambiguationData":[TD([[makeQuery(id+"F2.imprint","IMPRINT",EDGE,{"derivedFrom":subQ0}),1.0]])]});}
            var Q50;
            {var subQ0=sQuery(id+"F2.wireOp",EDGE,"E30.MirrorCS");Q50=makeQuery(id+"F2.imprint","IMPRINT",FACE,{"disambiguationData":[TD([[makeQuery(id+"F2.imprint","IMPRINT",EDGE,{"derivedFrom":subQ0}),-1.0]])]});}
            var Q51;
            {var subQ4=sQuery(id+"F2.wireOp",EDGE,"E54.MirrorCS");Q51=makeQuery(id+"F2.imprint","IMPRINT",FACE,{"disambiguationData":[TD([[makeQuery(id+"F2.imprint","IMPRINT",EDGE,{"derivedFrom":subQ4}),-1.0]])]});}
            var Q52;
            {var subQ4=sQuery(id+"F2.wireOp",EDGE,"E87.MirrorCS");Q52=makeQuery(id+"F2.imprint","IMPRINT",FACE,{"disambiguationData":[TD([[makeQuery(id+"F2.imprint","IMPRINT",EDGE,{"derivedFrom":subQ4}),-1.0]])]});}
            var Q53;
            {var subQ0=sQuery(id+"F2.wireOp",EDGE,"E88.MirrorCS");Q53=makeQuery(id+"F2.imprint","IMPRINT",FACE,{"disambiguationData":[TD([[makeQuery(id+"F2.imprint","IMPRINT",EDGE,{"derivedFrom":subQ0}),-1.0]])]});}
            var Q54;
            {var subQ0=sQuery(id+"F2.wireOp",EDGE,"E90.MirrorCS");Q54=makeQuery(id+"F2.imprint","IMPRINT",FACE,{"disambiguationData":[TD([[makeQuery(id+"F2.imprint","IMPRINT",EDGE,{"derivedFrom":subQ0}),-1.0]])]});}
            var Q55;
            {var subQ4=sQuery(id+"F2.wireOp",EDGE,"E91.MirrorCS");Q55=makeQuery(id+"F2.imprint","IMPRINT",FACE,{"disambiguationData":[TD([[makeQuery(id+"F2.imprint","IMPRINT",EDGE,{"derivedFrom":subQ4}),-1.0]])]});}
            var Q56;
            {var subQ3=sQuery(id+"F2.wireOp",EDGE,"E5.24.0.0");Q56=makeQuery(id+"F2.imprint","IMPRINT",FACE,{"disambiguationData":[TD([[makeQuery(id+"F2.imprint","IMPRINT",EDGE,{"derivedFrom":subQ3}),1.0]])]});}
            var Q57;
            {var subQ3=sQuery(id+"F2.wireOp",EDGE,"E98");Q57=makeQuery(id+"F2.imprint","IMPRINT",FACE,{"disambiguationData":[TD([[makeQuery(id+"F2.imprint","IMPRINT",EDGE,{"derivedFrom":subQ3}),-1.0]])]});}
            var Q58;
            {var subQ4=sQuery(id+"F2.wireOp",EDGE,"E100.MirrorCS");Q58=makeQuery(id+"F2.imprint","IMPRINT",FACE,{"disambiguationData":[TD([[makeQuery(id+"F2.imprint","IMPRINT",EDGE,{"derivedFrom":subQ4}),1.0]])]});}
            extrude(context, id + "F3", {"entities" : qUnion([Q0, Q1, Q2, Q3, Q4, Q5, Q6, Q7, Q8, Q9, Q10, Q11, Q12, Q13, Q14, Q15, Q16, Q17, Q18, Q19, Q20, Q21, Q22, Q23, Q24, Q25, Q26, Q27, Q28, Q29, Q30, Q31, Q32, Q33, Q34, Q35, Q36, Q37, Q38, Q39, Q40, Q41, Q42, Q43, Q44, Q45, Q46, Q47, Q48, Q49, Q50, Q51, Q52, Q53, Q54, Q55, Q56, Q57, Q58]), "operationType" : NewBodyOperationType.REMOVE, "oppositeDirection" : true, "depth" : 25.4 * mm});
        }
        {
            var Q0;
            Q0=qCreatedBy(makeId("Top.planeOp"),FACE);
            var sketch = newSketch(context, id + "F4", { "sketchPlane" : qUnion([Q0])});
            skLineSegment(sketch, "E102.bottom", {"start": v(-227.18, -45.02) * mm, "end": v(-23.98, -45.02) * mm});
            skLineSegment(sketch, "E102.top", {"start": v(-227.18, -248.22) * mm, "end": v(-23.98, -248.22) * mm});
            skLineSegment(sketch, "E102.left", {"start": v(-227.18, -45.02) * mm, "end": v(-227.18, -248.22) * mm});
            skLineSegment(sketch, "E102.right", {"start": v(-23.98, -45.02) * mm, "end": v(-23.98, -248.22) * mm});
            skSolve(sketch);
        }
        {
            var Q0;
            Q0=makeQuery(id+"F4.imprint","IMPRINT",FACE,{"disambiguationData":[TD([[makeQuery(id+"F4.imprint","IMPRINT",EDGE,{"derivedFrom":sQuery(id+"F4.wireOp",EDGE,"E102.bottom")}),-1.0]])]});
            extrude(context, id + "F5", {"entities" : qUnion([Q0]), "depth" : 5.08 * mm});
        }
    });
